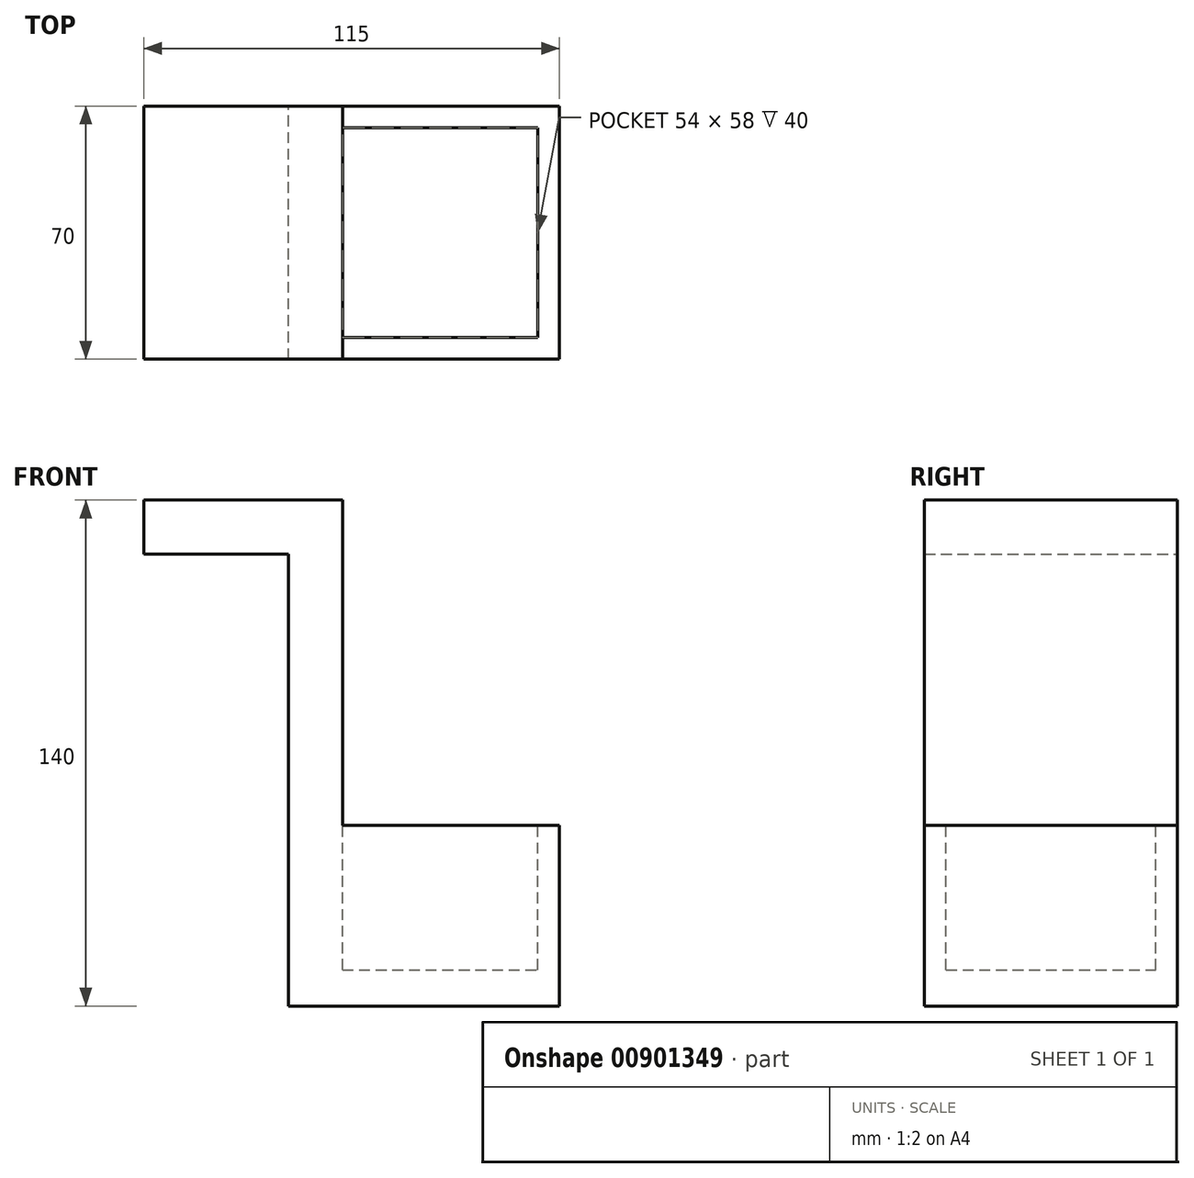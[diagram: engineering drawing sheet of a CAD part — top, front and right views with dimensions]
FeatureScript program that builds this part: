
annotation { "Feature Type Name" : "Feature", "Feature Type Description" : "" }
export const myFeature = defineFeature(function(context is Context, id is Id, definition is map)
    precondition{}
    {
        {
            var Q0;
            Q0=qCreatedBy(makeId("Front.planeOp"),FACE);
            var sketch = newSketch(context, id + "F0", { "sketchPlane" : qUnion([Q0])});
            skLineSegment(sketch, "E0.bottom", {"start": v(0, 0) * mm, "end": v(60, 0) * mm});
            skLineSegment(sketch, "E0.top", {"start": v(0, 50) * mm, "end": v(60, 50) * mm});
            skLineSegment(sketch, "E0.right", {"start": v(60, 0) * mm, "end": v(60, 50) * mm});
            skLineSegment(sketch, "E1.bottom", {"start": v(0, 0) * mm, "end": v(-15, 0) * mm});
            skLineSegment(sketch, "E1.top", {"start": v(0, 140) * mm, "end": v(-15, 140) * mm});
            skLineSegment(sketch, "E1.left", {"start": v(0, 50) * mm, "end": v(0, 140) * mm});
            skLineSegment(sketch, "E1.right", {"start": v(-15, 0) * mm, "end": v(-15, 125) * mm});
            skLineSegment(sketch, "E2.bottom", {"start": v(-15, 140) * mm, "end": v(-55, 140) * mm});
            skLineSegment(sketch, "E2.top", {"start": v(-15, 125) * mm, "end": v(-55, 125) * mm});
            skLineSegment(sketch, "E2.right", {"start": v(-55, 140) * mm, "end": v(-55, 125) * mm});
            skSolve(sketch);
        }
        {
            var Q0;
            Q0=makeQuery(id+"F0.imprint","IMPRINT",FACE,{"disambiguationData":[TD([[makeQuery(id+"F0.imprint","IMPRINT",EDGE,{"derivedFrom":sQuery(id+"F0.wireOp",EDGE,"E0.bottom")}),1.0]])]});
            extrude(context, id + "F1", {"entities" : qUnion([Q0]), "depth" : 70 * mm, "offsetDistance" : 25 * mm});
        }
        {
            var Q0;
            Q0=makeQuery(id+"F1.opExtrude","SWEPT_FACE",FACE,{"disambiguationData":[OSD([sQuery(id+"F0.wireOp",EDGE,"E0.top")])]});
            var sketch = newSketch(context, id + "F2", { "sketchPlane" : qUnion([Q0])});
            skLineSegment(sketch, "E3.bottom", {"start": v(0, -6) * mm, "end": v(54, -6) * mm});
            skLineSegment(sketch, "E3.top", {"start": v(0, -64) * mm, "end": v(54, -64) * mm});
            skLineSegment(sketch, "E3.left", {"start": v(0, -6) * mm, "end": v(0, -64) * mm});
            skLineSegment(sketch, "E3.right", {"start": v(54, -6) * mm, "end": v(54, -64) * mm});
            skSolve(sketch);
        }
        {
            var Q0;
            Q0=makeQuery(id+"F2.imprint","IMPRINT",FACE,{"disambiguationData":[TD([[makeQuery(id+"F2.imprint","IMPRINT",EDGE,{"derivedFrom":sQuery(id+"F2.wireOp",EDGE,"E3.bottom")}),-1.0]])]});
            extrude(context, id + "F3", {"entities" : qUnion([Q0]), "operationType" : NewBodyOperationType.REMOVE, "oppositeDirection" : true, "depth" : 40 * mm, "offsetDistance" : 25 * mm});
        }
    });
